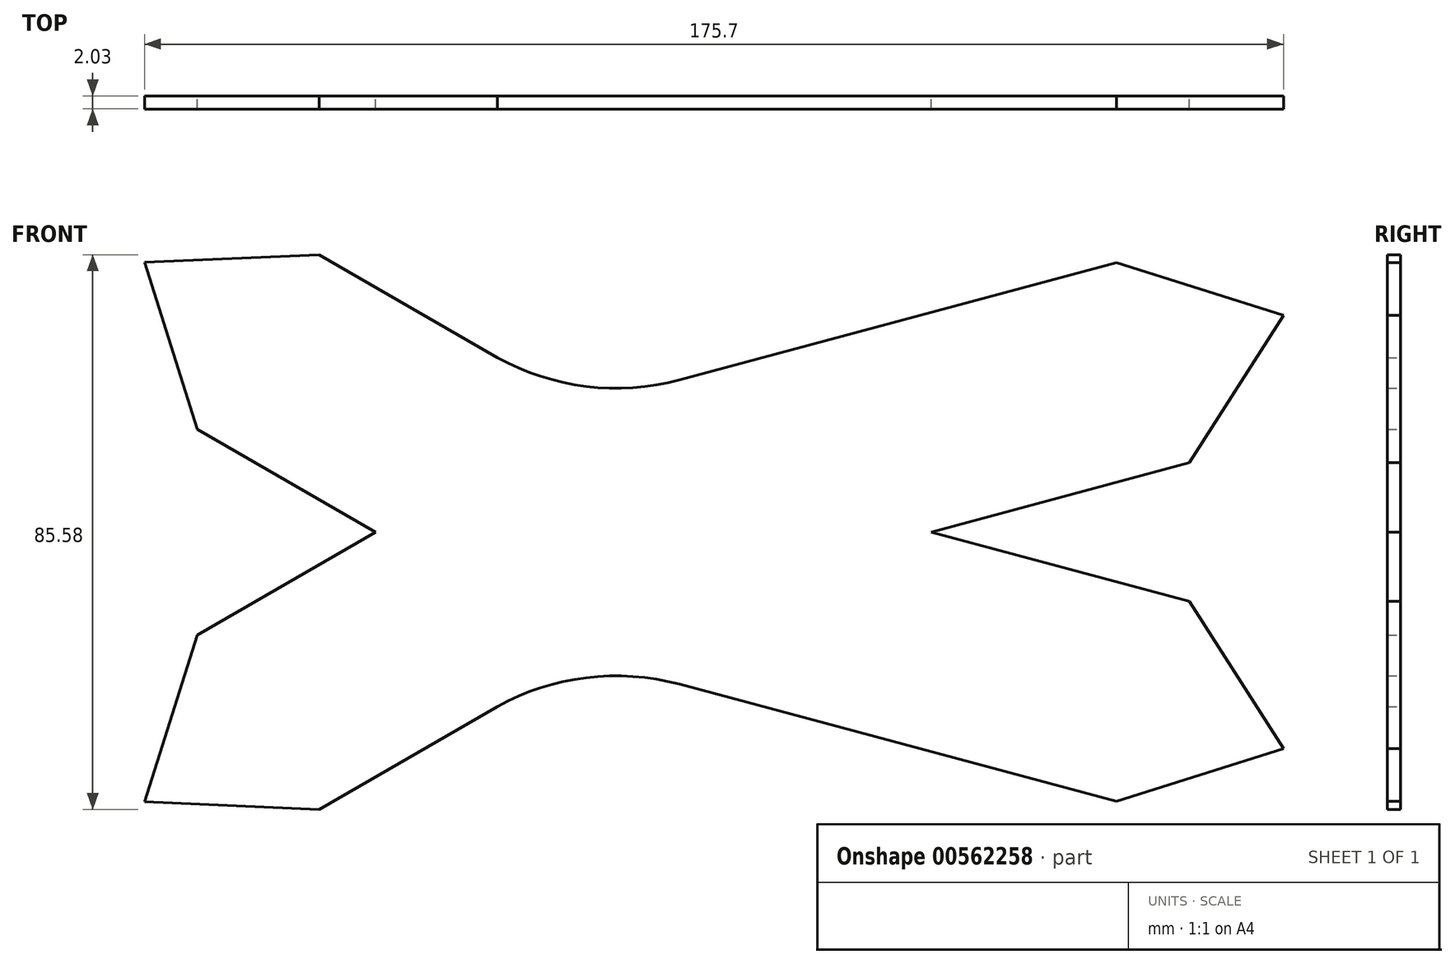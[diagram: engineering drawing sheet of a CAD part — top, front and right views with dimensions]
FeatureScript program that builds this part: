
annotation { "Feature Type Name" : "Feature", "Feature Type Description" : "" }
export const myFeature = defineFeature(function(context is Context, id is Id, definition is map)
    precondition{}
    {
        {
            var Q0;
            Q0=qCreatedBy(makeId("Front.planeOp"),FACE);
            var sketch = newSketch(context, id + "F0", { "sketchPlane" : qUnion([Q0])});
            skLineSegment(sketch, "E0", {"start": v(0, 0) * mm, "end": v(85.73, 0) * mm, "construction": true});
            skLineSegment(sketch, "E1", {"start": v(0, 0) * mm, "end": v(-27.5, 15.88) * mm});
            skLineSegment(sketch, "E2", {"start": v(-27.5, 15.87) * mm, "end": v(-35.61, 41.61) * mm});
            skLineSegment(sketch, "E3", {"start": v(-35.61, 41.61) * mm, "end": v(-8.65, 42.8) * mm});
            skLineSegment(sketch, "E4", {"start": v(-8.65, 42.8) * mm, "end": v(18.85, 26.92) * mm});
            skLineSegment(sketch, "E5", {"start": v(46.89, 23.48) * mm, "end": v(114.36, 41.56) * mm});
            skLineSegment(sketch, "E6", {"start": v(114.36, 41.56) * mm, "end": v(140.1, 33.44) * mm});
            skLineSegment(sketch, "E7", {"start": v(140.1, 33.44) * mm, "end": v(125.6, 10.68) * mm});
            skLineSegment(sketch, "E8", {"start": v(125.6, 10.68) * mm, "end": v(85.73, 0) * mm});
            skLineSegment(sketch, "E9", {"start": v(114.36, 41.56) * mm, "end": v(125.6, 10.68) * mm, "construction": true});
            skLineSegment(sketch, "E10", {"start": v(-8.65, 42.8) * mm, "end": v(-27.5, 15.87) * mm, "construction": true});
            skArc(sketch, "E11", {"start": v(18.85, 26.92) * mm, "mid": v(32.53, 22.47) * mm, "end": v(46.89, 23.48) * mm});
            skLineSegment(sketch, "E12.MirrorCS", {"start": v(-27.5, -15.87) * mm, "end": v(-35.61, -41.61) * mm});
            skArc(sketch, "E13.MirrorCS", {"start": v(18.85, -26.92) * mm, "mid": v(32.53, -22.47) * mm, "end": v(46.89, -23.48) * mm});
            skLineSegment(sketch, "E14.MirrorCS", {"start": v(-8.65, -42.8) * mm, "end": v(-27.5, -15.87) * mm, "construction": true});
            skLineSegment(sketch, "E15.MirrorCS", {"start": v(-35.61, -41.61) * mm, "end": v(-8.65, -42.8) * mm});
            skLineSegment(sketch, "E16.MirrorCS", {"start": v(140.1, -33.44) * mm, "end": v(125.6, -10.68) * mm});
            skLineSegment(sketch, "E17.MirrorCS", {"start": v(114.36, -41.56) * mm, "end": v(140.1, -33.44) * mm});
            skLineSegment(sketch, "E18.MirrorCS", {"start": v(46.89, -23.48) * mm, "end": v(114.36, -41.56) * mm});
            skLineSegment(sketch, "E19.MirrorCS", {"start": v(-8.65, -42.8) * mm, "end": v(18.85, -26.92) * mm});
            skLineSegment(sketch, "E20.MirrorCS", {"start": v(114.36, -41.56) * mm, "end": v(125.6, -10.68) * mm, "construction": true});
            skLineSegment(sketch, "E21.MirrorCS", {"start": v(0, 0) * mm, "end": v(-27.5, -15.88) * mm});
            skLineSegment(sketch, "E22.MirrorCS", {"start": v(125.6, -10.68) * mm, "end": v(85.73, 0) * mm});
            skSolve(sketch);
        }
        {
            var Q0;
            Q0 = qSketchRegion(id + "F0", true);
            extrude(context, id + "F1", {"entities" : qUnion([Q0]), "depth" : 2.03 * mm, "offsetDistance" : 25.4 * mm});
        }
    });
